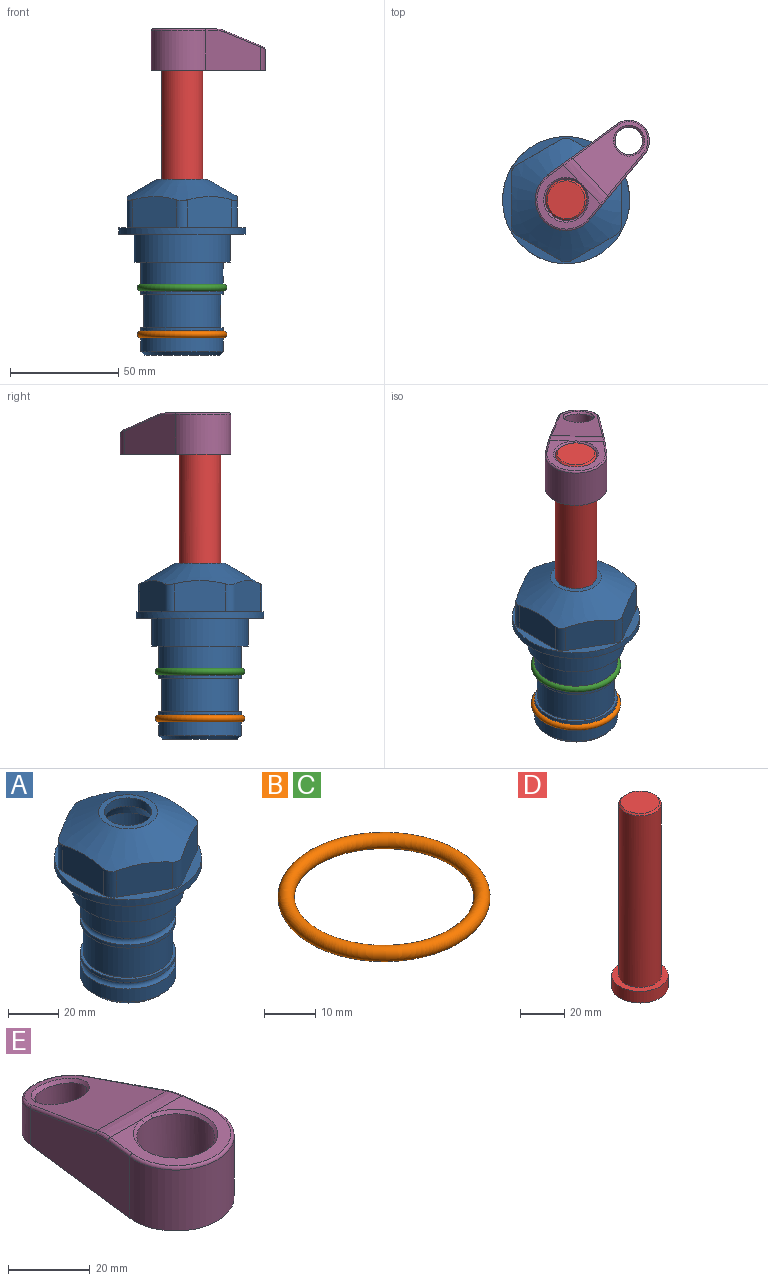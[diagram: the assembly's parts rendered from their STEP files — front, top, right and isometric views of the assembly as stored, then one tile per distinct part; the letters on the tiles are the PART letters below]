
ASSEMBLY  parts=5 mates=2
PART A: 36 faces, bbox 58.7x58.7x81 mm
  f0: cylinder r=17.78mm len=35.56mm, axis (0,0,1), area 1670.8mm2, adj f23,f24,f31
  f1: cylinder r=19.05mm len=38.1mm, axis (0,0,1), area 1191.9mm2, adj f26,f27,f30
  f2: plane 58.66x58.66mm, normal (0,0,-1), area 1150.6mm2, adj f3,f28
  f3: cylinder r=29.33mm len=58.66mm, axis (0,0,-1), area 585.1mm2, adj f2,f4
  f4: plane 58.66x58.66mm, normal (0,0,1), area 475.9mm2, adj f3,f5,f6,f7,f8,f9,f10,f11
  f5: plane 20.32x14.34mm, normal (-0.5,0.87,0), area 324.4mm2, adj f4,f15,f16,f17
  f6: plane 20.32x14.34mm, normal (0.5,0.87,0), area 324.4mm2, adj f4,f14,f15,f17
  f7: plane 23.48x14.34mm, normal (1,0,0), area 324.4mm2, adj f4,f13,f14,f17
  f8: plane 20.32x14.34mm, normal (0.5,-0.87,0), area 324.4mm2, adj f4,f12,f13,f17
  f9: plane 20.32x14.34mm, normal (-0.5,-0.87,0), area 324.4mm2, adj f4,f11,f12,f17
  f10: plane 23.48x14.34mm, normal (-1,0,0), area 324.4mm2, adj f4,f11,f16,f17
  f11: cylinder r=5.08mm len=12.85mm, axis (0,0,-1), area 67.2mm2, adj f4,f9,f10,f17
  f12: cylinder r=5.08mm len=12.85mm, axis (0,0,-1), area 67.2mm2, adj f4,f8,f9,f17
  f13: cylinder r=5.08mm len=12.85mm, axis (0,0,-1), area 67.2mm2, adj f4,f7,f8,f17
  f14: cylinder r=5.08mm len=12.85mm, axis (0,0,-1), area 67.2mm2, adj f4,f6,f7,f17
  f15: cylinder r=5.08mm len=12.85mm, axis (0,0,-1), area 67.2mm2, adj f4,f5,f6,f17
  f16: cylinder r=5.08mm len=12.85mm, axis (0,0,-1), area 67.2mm2, adj f4,f5,f10,f17
  f17: cone r=11.73mm half-angle=60deg, axis (0,0,-1), area 2071.8mm2, adj f5,f6,f7,f8,f9,f10,f11,f12
  f18: plane 23.46x23.46mm, normal (0,0,1), area 147.4mm2, adj f17,f35
  f19: plane 34.93x34.93mm, normal (0,0,-1), area 958mm2, adj f29
  f20: cylinder r=19.05mm len=38.1mm, axis (0,0,1), area 760.1mm2, adj f21,f29
  f21: torus R=19.05mm, axis (0,0,1), area 565.3mm2, adj f20,f22
  f22: cylinder r=19.05mm len=38.1mm, axis (0,0,1), area 190mm2, adj f21,f23
  f23: plane 38.1x38.1mm, normal (0,0,1), area 146.9mm2, adj f0,f22
  f24: plane 38.1x38.1mm, normal (0,0,-1), area 146.9mm2, adj f0,f25
  f25: cylinder r=19.05mm len=38.1mm, axis (0,0,1), area 190mm2, adj f24,f26
  f26: torus R=19.05mm, axis (0,0,1), area 565.3mm2, adj f1,f25
  f27: plane 44.45x44.45mm, normal (0,0,-1), area 411.7mm2, adj f1,f28
  f28: cylinder r=22.23mm len=44.45mm, axis (0,0,1), area 1773.5mm2, adj f2,f27
  f29: cone r=19.05mm half-angle=45deg, axis (0,0,1), area 257.5mm2, adj f19,f20
  f30: cylinder r=3.17mm len=6.75mm, axis (-1,0,0), area 128mm2, adj f1,f33
  f31: cylinder r=3.17mm len=6.35mm, axis (-1,0,0), area 102.5mm2, adj f0,f33
  f32: plane 25.4x25.4mm, normal (0,0,1), area 506.7mm2, adj f33
  f33: cylinder r=12.7mm len=66.42mm, axis (0,0,-1), area 5236.2mm2, adj f30,f31,f32,f34
  f34: cone r=9.53mm half-angle=30deg, axis (0,0,-1), area 443.4mm2, adj f33,f35
  f35: cylinder r=9.53mm len=19.05mm, axis (0,0,-1), area 240.9mm2, adj f18,f34
PART B: 1 faces, bbox 44.7x44.7x3.2 mm
  f0: torus R=19.05mm, axis (0,0,1), area 1193.9mm2
PART C: same geometry as B
PART D: 6 faces, bbox 25.4x25.4x101.6 mm
  f0: plane 17.46x17.46mm, normal (0,0,1), area 239.5mm2, adj f5
  f1: plane 25.4x25.4mm, normal (0,0,-1), area 506.7mm2, adj f2
  f2: cylinder r=12.7mm len=25.4mm, axis (0,0,1), area 506.7mm2, adj f1,f3
  f3: plane 25.4x25.4mm, normal (0,0,1), area 221.7mm2, adj f2,f4
  f4: cylinder r=9.53mm len=94.46mm, axis (0,0,1), area 5653mm2, adj f3,f5
  f5: cone r=8.73mm half-angle=45deg, axis (0,0,-1), area 64.4mm2, adj f0,f4
PART E: 31 faces, bbox 31.7x65.5x19.8 mm
  f0: plane 39.12x18.26mm, normal (0.99,0.12,0), area 612.2mm2, adj f1,f4,f7,f11,f13,f15
  f1: cylinder r=9.53mm len=18.91mm, axis (0,0,-1), area 296.1mm2, adj f0,f2,f7,f17
  f2: plane 39.12x18.26mm, normal (-0.99,0.12,0), area 612.2mm2, adj f1,f4,f7,f12,f14,f16
  f3: cylinder r=6.35mm len=12.7mm, axis (0,0,-1), area 362.4mm2, adj f7,f18
  f4: cylinder r=14.29mm len=28.58mm, axis (0,0,-1), area 882.2mm2, adj f0,f2,f7,f10
  f5: cylinder r=9.53mm len=19.05mm, axis (0,0,-1), area 1092.6mm2, adj f7,f19,f20
  f6: plane 26.99x23.69mm, normal (0,0,1), area 216.2mm2, adj f9,f10,f11,f12,f19
  f7: plane 63.5x28.58mm, normal (0,0,-1), area 661.8mm2, adj f0,f1,f2,f3,f4,f5,f22,f23
  f8: plane 33.52x23.6mm, normal (0,0.26,0.97), area 486mm2, adj f9,f15,f16,f17,f18
  f9: cylinder r=19.05mm len=24.72mm, axis (1,0,0), area 120.4mm2, adj f6,f8,f13,f14,f20
  f10: torus R=13.49mm, axis (0,0,1), area 59mm2, adj f4,f6,f11,f12
  f11: cylinder r=0.79mm len=8.67mm, axis (0.12,-0.99,0), area 10.8mm2, adj f0,f6,f10,f13
  f12: cylinder r=0.79mm len=8.67mm, axis (0.12,0.99,0), area 10.8mm2, adj f2,f6,f10,f14
  f13: bspline ~4.95x1.42mm, area 6.1mm2, adj f0,f9,f11,f15
  f14: bspline ~4.95x1.42mm, area 6.1mm2, adj f2,f9,f12,f16
  f15: cylinder r=0.79mm len=25.95mm, axis (0.12,-0.96,0.26), area 32.9mm2, adj f0,f8,f13,f17
  f16: cylinder r=0.79mm len=25.95mm, axis (0.12,0.96,-0.26), area 32.9mm2, adj f2,f8,f14,f17
  f17: bspline ~18.91x8.38mm, area 30mm2, adj f1,f8,f15,f16
  f18: bspline ~14.29x14.29mm, area 48.3mm2, adj f3,f8
  f19: cone r=9.53mm half-angle=45deg, axis (0,0,1), area 66.5mm2, adj f5,f6,f20
  f20: bspline ~3.22x0.96mm, area 3.5mm2, adj f5,f9,f19
  f21: plane 2.75x2.72mm, normal (0,0,-1), area 2.9mm2, adj f23,f25,f28
  f22: plane 23.05x15.88mm, normal (-0.99,-0.12,0), area 323.6mm2, adj f7,f25,f26,f27,f28,f29
  f23: plane 23.05x15.88mm, normal (0.99,-0.12,0), area 323.6mm2, adj f7,f21,f25,f27,f28,f30
  f24: cylinder r=9.53mm len=10.69mm, axis (0,0,-1), area 114.7mm2, adj f7,f27,f29,f30
  f25: cylinder r=12.7mm len=20.59mm, axis (0,0,-1), area 381.1mm2, adj f7,f21,f22,f23,f26,f28
  f26: plane 2.75x2.72mm, normal (0,0,-1), area 2.9mm2, adj f22,f25,f28
  f27: plane 19.72x18.37mm, normal (0,-0.26,-0.97), area 291.8mm2, adj f22,f23,f24,f28,f29,f30
  f28: cylinder r=15.88mm len=19.92mm, axis (1,0,0), area 54.8mm2, adj f21,f22,f23,f25,f26,f27
  f29: cylinder r=1.59mm len=11mm, axis (0,0,-1), area 34.7mm2, adj f7,f22,f24,f27
  f30: cylinder r=1.59mm len=11mm, axis (0,0,-1), area 34.7mm2, adj f7,f23,f24,f27
PLACE A at identity fixed
PLACE B t=(0,0,-21.59)mm
PLACE C at identity
PLACE D rot(axis=(0,0,-1),46.7deg) t=(0,0,31.34)mm
PLACE E rot(axis=(0,0,-1),46.7deg) t=(0,0,31.34)mm
MATE fastened B.f0 <-> A.f0  axis (0,0,1) through (0,0,-46.1)mm
MATE cylindrical D.f2 <-> A.f0  axis (0,0,-1) through (0,0,-6.76)mm
